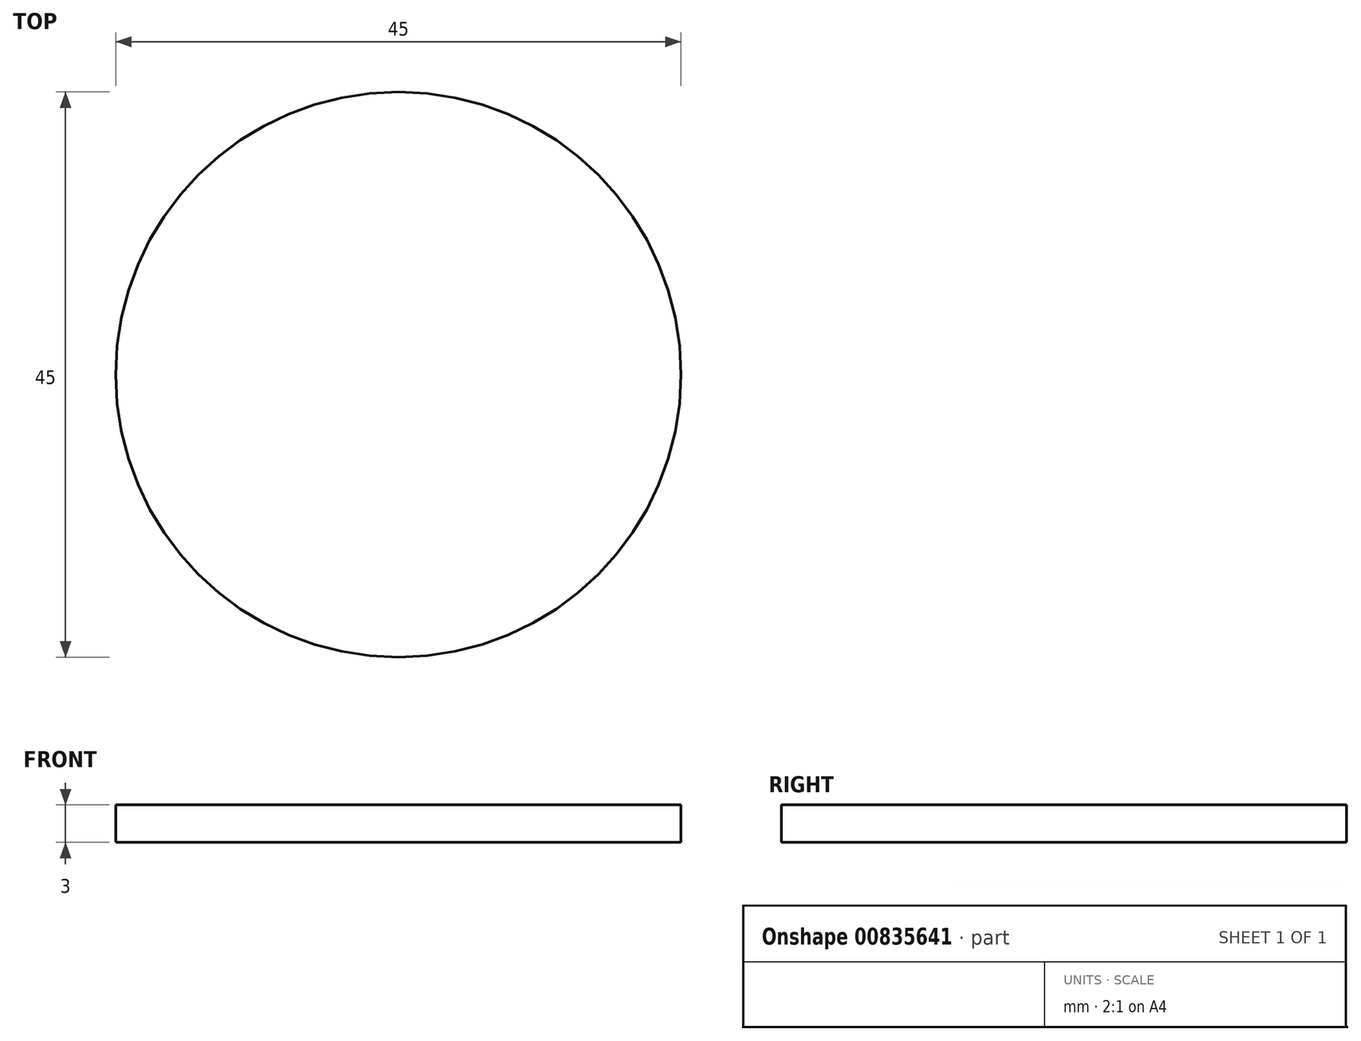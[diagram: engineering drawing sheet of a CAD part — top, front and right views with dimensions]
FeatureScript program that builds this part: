
annotation { "Feature Type Name" : "Feature", "Feature Type Description" : "" }
export const myFeature = defineFeature(function(context is Context, id is Id, definition is map)
    precondition{}
    {
        {
            var Q0;
            Q0=qCreatedBy(makeId("Top.planeOp"),FACE);
            var sketch = newSketch(context, id + "F0", { "sketchPlane" : qUnion([Q0])});
            skCircle(sketch, "E0", {"center": v(0, 0) * mm, "radius": 22.5 * mm});
            skSolve(sketch);
        }
        {
            var Q0;
            Q0 = qSketchRegion(id + "F0", true);
            extrude(context, id + "F1", {"entities" : qUnion([Q0]), "depth" : 3 * mm, "offsetDistance" : 25.4 * mm});
        }
    });
